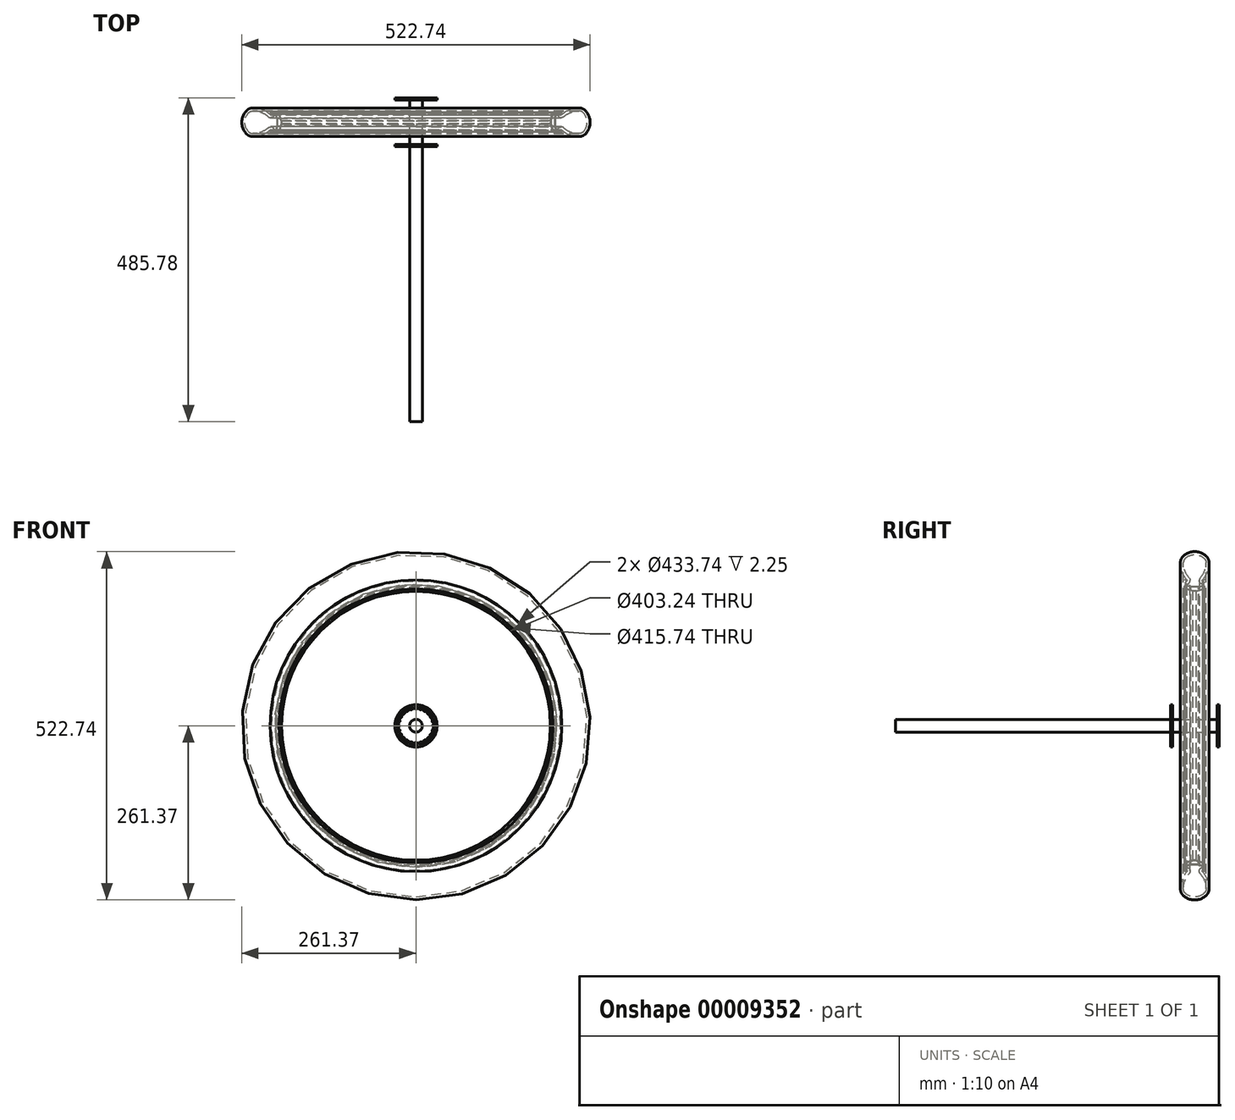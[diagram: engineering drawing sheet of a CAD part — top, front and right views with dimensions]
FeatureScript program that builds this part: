
annotation { "Feature Type Name" : "Feature", "Feature Type Description" : "" }
export const myFeature = defineFeature(function(context is Context, id is Id, definition is map)
    precondition{}
    {
        {
            var Q0;
            Q0=qCreatedBy(makeId("Front.planeOp"),FACE);
            var sketch = newSketch(context, id + "F0", { "sketchPlane" : qUnion([Q0])});
            skCircle(sketch, "E0", {"center": v(0, 0) * mm, "radius": 31.75 * mm});
            skCircle(sketch, "E1", {"center": v(0, 0) * mm, "radius": 9.53 * mm});
            skSolve(sketch);
        }
        {
            var Q0;
            Q0=qSketchRegion(id+"F0",true);
            extrude(context, id + "F1", {"entities" : qUnion([Q0]), "depth" : 3.17 * mm});
        }
        {
            var Q0;
            Q0=qCreatedBy(makeId("Right.planeOp"),FACE);
            var sketch = newSketch(context, id + "F2", { "sketchPlane" : qUnion([Q0])});
            skLineSegment(sketch, "E2", {"start": v(-31.75, 0) * mm, "end": v(31.75, 0) * mm, "construction": true});
            skLineSegment(sketch, "E3", {"start": v(-31.75, 27.19) * mm, "end": v(31.75, 27.19) * mm, "construction": true});
            skPoint(sketch, "E4", {"position": v(-3.18, 28.57) * mm});
            skLineSegment(sketch, "E5", {"start": v(-3.18, 31.75) * mm, "end": v(0, 31.75) * mm, "construction": true});
            skSolve(sketch);
        }
        {
            var Q0;
            Q0=qCreatedBy(makeId("Right.planeOp"),FACE);
            var sketch = newSketch(context, id + "F3", { "sketchPlane" : qUnion([Q0])});
            skLineSegment(sketch, "E6", {"start": v(-3.18, 27.19) * mm, "end": v(-3.18, 29.37) * mm});
            skLineSegment(sketch, "E7", {"start": v(-3.18, 29.37) * mm, "end": v(-2.7, 28.57) * mm});
            skLineSegment(sketch, "E8", {"start": v(-2.7, 28.57) * mm, "end": v(-0.48, 28.57) * mm});
            skLineSegment(sketch, "E9", {"start": v(-0.48, 28.57) * mm, "end": v(0, 29.37) * mm});
            skLineSegment(sketch, "E10", {"start": v(0, 29.37) * mm, "end": v(0, 27.19) * mm});
            skLineSegment(sketch, "E11", {"start": v(0, 27.19) * mm, "end": v(-3.18, 27.19) * mm});
            skLineSegment(sketch, "E12", {"start": v(-1.59, 27.19) * mm, "end": v(-1.59, 31.75) * mm, "construction": true});
            skSolve(sketch);
        }
        {
            var Q0;
            Q0=qSketchRegion(id+"F3",true);
            var Q1;
            Q1=sQuery(id+"F2.wireOp",EDGE,"E3");
            revolve(context, id + "F4", {"entities" : qUnion([Q0]), "axis" : qUnion([Q1]), "revolveType" : RevolveType.FULL, "oppositeDirection" : true});
        }
        {
            var Q0;
            Q0=makeQuery(id+"F4.opRevolve","SWEPT_BODY",BODY,{"disambiguationData":[OSD([sQuery(id+"F3.wireOp",EDGE,"E6"),sQuery(id+"F3.wireOp",EDGE,"E7"),sQuery(id+"F3.wireOp",EDGE,"E8"),sQuery(id+"F3.wireOp",EDGE,"E9"),sQuery(id+"F3.wireOp",EDGE,"E10"),sQuery(id+"F3.wireOp",EDGE,"E11")])]});
            var Q1;
            Q1=sQuery(id+"F2.wireOp",EDGE,"E2");
            circularPattern(context, id + "F5", {"operationType" : NewBodyOperationType.REMOVE, "entities" : qUnion([Q0]), "axis" : qUnion([Q1]), "angle" : 360 * degree, "instanceCount" : round(24), "equalSpace" : true});
        }
        {
            var Q0;
            Q0=makeQuery(id+"F1.opExtrude","SWEPT_BODY",BODY,{"disambiguationData":[OSD([sQuery(id+"F0.wireOp",EDGE,"E0"),sQuery(id+"F0.wireOp",EDGE,"E1")])]});
            var Q1;
            Q1=sQuery(id+"F2.wireOp",EDGE,"E2");
            transform(context, id + "F6", {"entities" : qUnion([Q0]), "transformType" : TransformType.TRANSLATION_DISTANCE, "transformDirection" : qUnion([Q1]), "distance" : 69.85 * mm, "makeCopy" : true});
        }
        {
            var Q0;
            Q0=makeQuery(id+"F6.opPattern","COPY",BODY,{"derivedFrom":makeQuery(id+"F1.opExtrude","SWEPT_BODY",BODY,{"disambiguationData":[OSD([sQuery(id+"F0.wireOp",EDGE,"E0"),sQuery(id+"F0.wireOp",EDGE,"E1")])]}),"instanceName":"1"});
            var Q1;
            Q1=sQuery(id+"F2.wireOp",EDGE,"E2");
            transform(context, id + "F7", {"entities" : qUnion([Q0]), "transformType" : TransformType.ROTATION, "transformAxis" : qUnion([Q1]), "angle" : 7.5 * degree, "makeCopy" : false});
        }
        {
            var Q0;
            Q0=qCreatedBy(makeId("Right.planeOp"),FACE);
            var sketch = newSketch(context, id + "F8", { "sketchPlane" : qUnion([Q0])});
            skLineSegment(sketch, "E13", {"start": v(0, 0) * mm, "end": v(66.68, 0) * mm, "construction": true});
            skLineSegment(sketch, "E14", {"start": v(33.34, 0) * mm, "end": v(33.34, 218.87) * mm, "construction": true});
            skSolve(sketch);
        }
        {
            var Q0;
            Q0=qCreatedBy(makeId("Front.planeOp"),FACE);
            var Q1;
            Q1=sQuery(id+"F8.wireOp",VERTEX,"E14.start");
            cPlane(context, id + "F9", {"entities" : qUnion([Q0, Q1]), "cplaneType" : CPlaneType.PLANE_POINT, "offset" : 150 * mm, "width" : 150 * mm, "height" : 150 * mm});
        }
        {
            var Q0;
            Q0=qCreatedBy(id+"F9.planeOp",FACE);
            var sketch = newSketch(context, id + "F10", { "sketchPlane" : qUnion([Q0])});
            skCircle(sketch, "E15", {"center": v(0, 0) * mm, "radius": 218.87 * mm, "construction": true});
            skSolve(sketch);
        }
        {
            var Q0;
            Q0=qCreatedBy(makeId("Right.planeOp"),FACE);
            var sketch = newSketch(context, id + "F11", { "sketchPlane" : qUnion([Q0])});
            skLineSegment(sketch, "E16", {"start": v(33.34, 201.62) * mm, "end": v(30.84, 201.62) * mm});
            skLineSegment(sketch, "E17", {"start": v(18.34, 218.87) * mm, "end": v(21.59, 218.87) * mm});
            skLineSegment(sketch, "E18", {"start": v(18.34, 218.87) * mm, "end": v(18.34, 205.53) * mm});
            skLineSegment(sketch, "E19", {"start": v(18.34, 205.53) * mm, "end": v(30.84, 201.62) * mm});
            skLineSegment(sketch, "E20", {"start": v(21.59, 218.87) * mm, "end": v(21.59, 216.87) * mm});
            skLineSegment(sketch, "E21", {"start": v(21.59, 216.87) * mm, "end": v(19.34, 216.87) * mm});
            skLineSegment(sketch, "E22", {"start": v(19.34, 216.87) * mm, "end": v(19.34, 211.37) * mm});
            skLineSegment(sketch, "E23", {"start": v(19.34, 211.37) * mm, "end": v(27.34, 208.87) * mm});
            skLineSegment(sketch, "E24", {"start": v(27.34, 208.87) * mm, "end": v(33.34, 208.87) * mm});
            skLineSegment(sketch, "E25", {"start": v(33.34, 207.87) * mm, "end": v(27.18, 207.87) * mm});
            skLineSegment(sketch, "E26", {"start": v(27.18, 207.87) * mm, "end": v(19.34, 210.32) * mm});
            skLineSegment(sketch, "E27", {"start": v(19.34, 210.32) * mm, "end": v(19.34, 206.26) * mm});
            skLineSegment(sketch, "E28", {"start": v(19.34, 206.26) * mm, "end": v(31, 202.62) * mm});
            skLineSegment(sketch, "E29", {"start": v(31, 202.62) * mm, "end": v(33.34, 202.62) * mm});
            skLineSegment(sketch, "E30", {"start": v(19.34, 214.12) * mm, "end": v(18.34, 214.12) * mm, "construction": true});
            skLineSegment(sketch, "E31", {"start": v(23.34, 210.12) * mm, "end": v(23.04, 209.17) * mm, "construction": true});
            skLineSegment(sketch, "E32", {"start": v(25.16, 204.44) * mm, "end": v(24.87, 203.49) * mm, "construction": true});
            skLineSegment(sketch, "E33", {"start": v(30.34, 208.87) * mm, "end": v(30.34, 207.87) * mm, "construction": true});
            skLineSegment(sketch, "E34", {"start": v(32.16, 202.62) * mm, "end": v(32.16, 201.62) * mm, "construction": true});
            skLineSegment(sketch, "E35", {"start": v(33.34, 218.87) * mm, "end": v(33.34, 208.87) * mm, "construction": true});
            skLineSegment(sketch, "E36.0.MirrorCS", {"start": v(39.34, 208.87) * mm, "end": v(33.34, 208.87) * mm});
            skLineSegment(sketch, "E37.0.MirrorCS", {"start": v(47.34, 211.37) * mm, "end": v(39.34, 208.87) * mm});
            skLineSegment(sketch, "E38.0.MirrorCS", {"start": v(47.34, 216.87) * mm, "end": v(47.34, 211.37) * mm});
            skLineSegment(sketch, "E39.0.MirrorCS", {"start": v(45.09, 216.87) * mm, "end": v(47.34, 216.87) * mm});
            skLineSegment(sketch, "E40.0.MirrorCS", {"start": v(45.09, 218.87) * mm, "end": v(45.09, 216.87) * mm});
            skLineSegment(sketch, "E41.0.MirrorCS", {"start": v(48.34, 218.87) * mm, "end": v(45.09, 218.87) * mm});
            skLineSegment(sketch, "E42.0.MirrorCS", {"start": v(48.34, 218.87) * mm, "end": v(48.34, 205.53) * mm});
            skLineSegment(sketch, "E43.0.MirrorCS", {"start": v(48.34, 205.53) * mm, "end": v(35.84, 201.62) * mm});
            skLineSegment(sketch, "E44.0.MirrorCS", {"start": v(33.34, 201.62) * mm, "end": v(35.84, 201.62) * mm});
            skLineSegment(sketch, "E45.0.MirrorCS", {"start": v(35.68, 202.62) * mm, "end": v(33.34, 202.62) * mm});
            skLineSegment(sketch, "E46.0.MirrorCS", {"start": v(47.34, 206.26) * mm, "end": v(35.68, 202.62) * mm});
            skLineSegment(sketch, "E47.0.MirrorCS", {"start": v(47.34, 210.32) * mm, "end": v(47.34, 206.26) * mm});
            skLineSegment(sketch, "E48.0.MirrorCS", {"start": v(39.5, 207.87) * mm, "end": v(47.34, 210.32) * mm});
            skLineSegment(sketch, "E49.0.MirrorCS", {"start": v(33.34, 207.87) * mm, "end": v(39.5, 207.87) * mm});
            skSolve(sketch);
        }
        {
            var Q0;
            Q0=qSketchRegion(id+"F11",true);
            var Q1;
            Q1=sQuery(id+"F8.wireOp",EDGE,"E13");
            revolve(context, id + "F12", {"entities" : qUnion([Q0]), "axis" : qUnion([Q1]), "revolveType" : RevolveType.FULL});
        }
        {
            var Q0;
            Q0=qCreatedBy(makeId("Right.planeOp"),FACE);
            var sketch = newSketch(context, id + "F13", { "sketchPlane" : qUnion([Q0])});
            skArc(sketch, "E50", {"start": v(21, 216.8) * mm, "mid": v(19.41, 214.05) * mm, "end": v(22.16, 212.46) * mm});
            skArc(sketch, "E51", {"start": v(21, 216.8) * mm, "mid": v(21.88, 217.64) * mm, "end": v(21.63, 218.83) * mm});
            skLineSegment(sketch, "E52", {"start": v(18.34, 261.37) * mm, "end": v(48.34, 261.37) * mm, "construction": true});
            skLineSegment(sketch, "E53", {"start": v(11.84, 261.37) * mm, "end": v(11.84, 218.87) * mm, "construction": true});
            skLineSegment(sketch, "E54", {"start": v(11.84, 244.87) * mm, "end": v(33.34, 244.87) * mm, "construction": true});
            skArc(sketch, "E55", {"start": v(11.84, 244.87) * mm, "mid": v(14.37, 230.96) * mm, "end": v(21.63, 218.83) * mm});
            skArc(sketch, "E56", {"start": v(33.34, 261.37) * mm, "mid": v(23.72, 259.45) * mm, "end": v(15.59, 253.98) * mm});
            skArc(sketch, "E57", {"start": v(15.59, 253.98) * mm, "mid": v(12.81, 249.8) * mm, "end": v(11.84, 244.87) * mm});
            skArc(sketch, "E58.0", {"start": v(22.16, 212.46) * mm, "mid": v(26.18, 216.33) * mm, "end": v(25, 221.79) * mm});
            skArc(sketch, "E58.1", {"start": v(16.33, 244.87) * mm, "mid": v(18.57, 232.54) * mm, "end": v(25, 221.79) * mm});
            skArc(sketch, "E58.2", {"start": v(18.77, 250.81) * mm, "mid": v(16.96, 248.09) * mm, "end": v(16.33, 244.87) * mm});
            skArc(sketch, "E58.3", {"start": v(33.34, 256.88) * mm, "mid": v(25.45, 255.3) * mm, "end": v(18.77, 250.81) * mm});
            skLineSegment(sketch, "E59", {"start": v(33.34, 261.37) * mm, "end": v(33.34, 218.87) * mm, "construction": true});
            skArc(sketch, "E60.0.MirrorCS", {"start": v(33.34, 261.37) * mm, "mid": v(42.95, 259.45) * mm, "end": v(51.09, 253.98) * mm});
            skArc(sketch, "E61.0.MirrorCS", {"start": v(51.09, 253.98) * mm, "mid": v(53.86, 249.8) * mm, "end": v(54.84, 244.87) * mm});
            skArc(sketch, "E62.0.MirrorCS", {"start": v(54.84, 244.87) * mm, "mid": v(52.3, 230.96) * mm, "end": v(45.05, 218.83) * mm});
            skArc(sketch, "E63.0.MirrorCS", {"start": v(45.67, 216.8) * mm, "mid": v(44.8, 217.64) * mm, "end": v(45.05, 218.83) * mm});
            skArc(sketch, "E64.0.MirrorCS", {"start": v(45.67, 216.8) * mm, "mid": v(47.26, 214.05) * mm, "end": v(44.52, 212.46) * mm});
            skArc(sketch, "E65.0.MirrorCS", {"start": v(44.52, 212.46) * mm, "mid": v(40.5, 216.33) * mm, "end": v(41.67, 221.79) * mm});
            skArc(sketch, "E66.0.MirrorCS", {"start": v(50.35, 244.87) * mm, "mid": v(48.1, 232.54) * mm, "end": v(41.67, 221.79) * mm});
            skArc(sketch, "E67.0.MirrorCS", {"start": v(47.9, 250.81) * mm, "mid": v(49.71, 248.09) * mm, "end": v(50.35, 244.87) * mm});
            skArc(sketch, "E68.0.MirrorCS", {"start": v(33.34, 256.88) * mm, "mid": v(41.23, 255.3) * mm, "end": v(47.9, 250.81) * mm});
            skSolve(sketch);
        }
        {
            var Q0;
            Q0=qSketchRegion(id+"F13",true);
            var Q1;
            Q1=sQuery(id+"F8.wireOp",EDGE,"E13");
            revolve(context, id + "F14", {"entities" : qUnion([Q0]), "axis" : qUnion([Q1]), "revolveType" : RevolveType.FULL});
        }
        {
            var Q0;
            Q0=makeQuery(id+"F6.opPattern","COPY",FACE,{"derivedFrom":makeQuery(id+"F1.opExtrude","CAP_FACE",FACE,{"disambiguationData":[OSD([sQuery(id+"F0.wireOp",EDGE,"E0"),sQuery(id+"F0.wireOp",EDGE,"E1")])],"isStart":true}),"instanceName":"1"});
            var sketch = newSketch(context, id + "F15", { "sketchPlane" : qUnion([Q0])});
            skCircle(sketch, "E69", {"center": v(0, 0) * mm, "radius": 9.53 * mm});
            skSolve(sketch);
        }
        {
            var Q0;
            Q0 = qSketchRegion(id + "F15", true);
            extrude(context, id + "F16", {"entities" : qUnion([Q0]), "oppositeDirection" : true, "depth" : 485.77 * mm});
        }
    });
